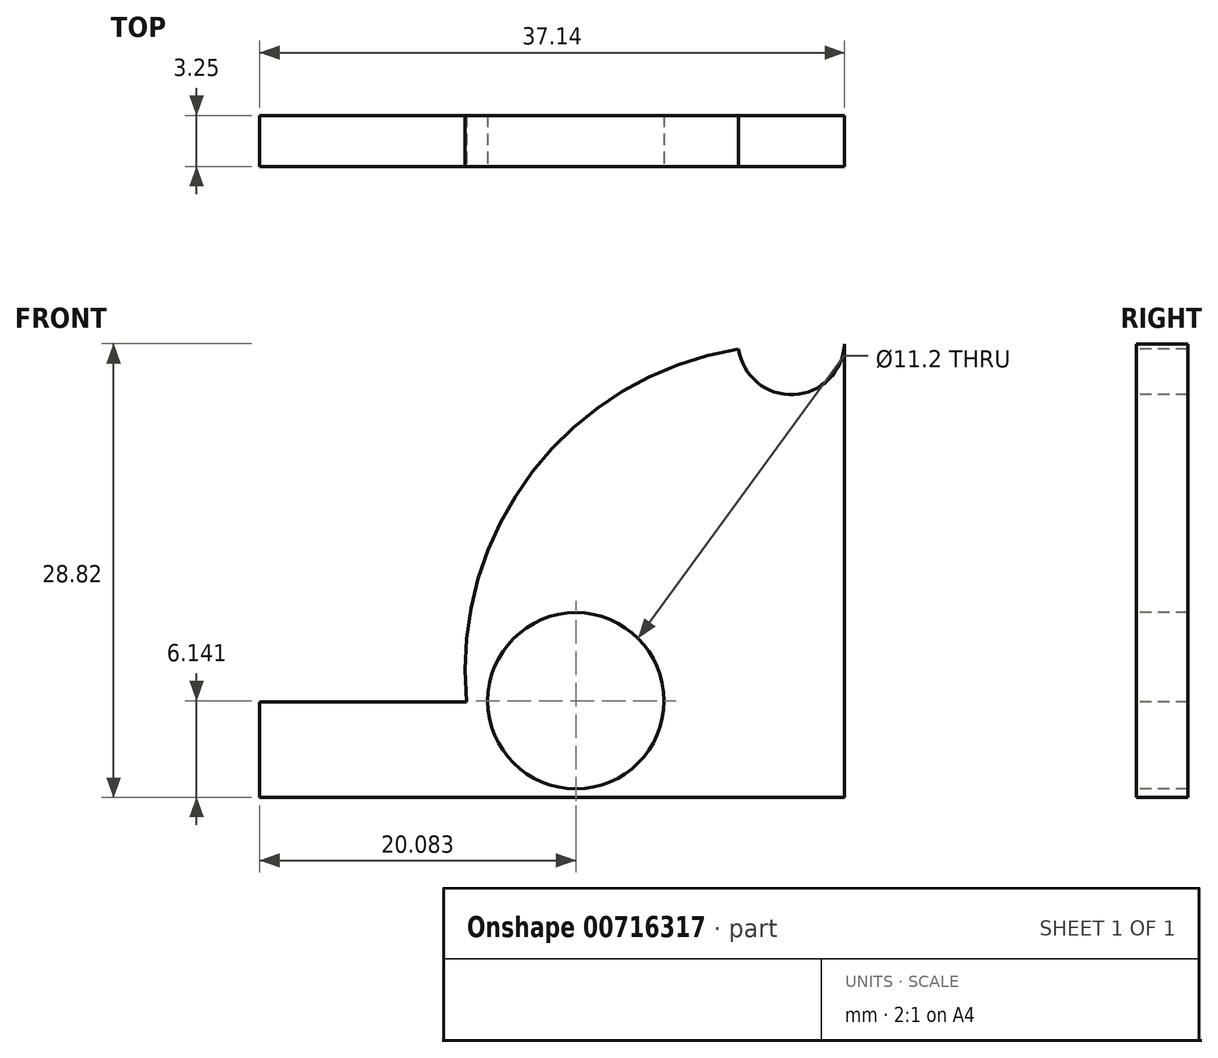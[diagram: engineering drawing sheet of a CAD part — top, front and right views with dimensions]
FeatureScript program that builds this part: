
annotation { "Feature Type Name" : "Feature", "Feature Type Description" : "" }
export const myFeature = defineFeature(function(context is Context, id is Id, definition is map)
    precondition{}
    {
        {
            var Q0;
            Q0=qCreatedBy(makeId("Front.planeOp"),FACE);
            var sketch = newSketch(context, id + "F0", { "sketchPlane" : qUnion([Q0])});
            skLineSegment(sketch, "E0", {"start": v(-17.05, -6.06) * mm, "end": v(20.1, -6.06) * mm});
            skLineSegment(sketch, "E1", {"start": v(20.1, -6.06) * mm, "end": v(20.1, 22.76) * mm});
            skLineSegment(sketch, "E2", {"start": v(-17.05, -6.06) * mm, "end": v(-17.05, 0) * mm});
            skLineSegment(sketch, "E3", {"start": v(-17.05, 0) * mm, "end": v(-3.92, 0) * mm});
            skArc(sketch, "E4", {"start": v(13.37, 22.44) * mm, "mid": v(0.29, 14.64) * mm, "end": v(-3.92, 0) * mm});
            skCircle(sketch, "E5", {"center": v(16.72, 22.9) * mm, "radius": 3.38 * mm});
            skPoint(sketch, "E5.third.point", {"position": v(16.9, 26.28) * mm});
            skFitSpline(sketch, "E6", {"points": [v(12.39, 22.25) * mm, v(14.8, 18.64) * mm, v(18.5, 18.19) * mm, v(20.1, 16.75) * mm], "startDerivative": vector(4.83, -12.05) * mm, "endDerivative": vector(4.66, -6.77) * mm});
            skLineSegment(sketch, "E7.bottom", {"start": v(-17.05, -0.6) * mm, "end": v(-16.21, -0.6) * mm});
            skLineSegment(sketch, "E7.top", {"start": v(-17.05, -5.27) * mm, "end": v(-16.21, -5.27) * mm});
            skLineSegment(sketch, "E7.left", {"start": v(-17.05, -0.6) * mm, "end": v(-17.05, -5.27) * mm});
            skLineSegment(sketch, "E7.right", {"start": v(-16.21, -0.6) * mm, "end": v(-16.21, -5.27) * mm});
            skCircle(sketch, "E8", {"center": v(3.03, 0.08) * mm, "radius": 5.6 * mm});
            skPoint(sketch, "E8.first.point", {"position": v(-2.56, 0) * mm});
            skPoint(sketch, "E8.second.point", {"position": v(8.63, 0) * mm});
            skPoint(sketch, "E8.third.point", {"position": v(5.15, 5.26) * mm});
            skCircle(sketch, "E9", {"center": v(3.03, 0.07) * mm, "radius": 4.71 * mm});
            skSolve(sketch);
        }
        {
            var Q0;
            Q0=makeQuery(id+"F0.imprint","IMPRINT",FACE,{"disambiguationData":[TD([[makeQuery(id+"F0.imprint","IMPRINT",EDGE,{"derivedFrom":sQuery(id+"F0.wireOp",EDGE,"E7.bottom")}),-1.0]])]});
            var Q1;
            {var subQ4=sQuery(id+"F0.wireOp",EDGE,"E0");Q1=makeQuery(id+"F0.imprint","IMPRINT",FACE,{"disambiguationData":[TD([[makeQuery(id+"F0.imprint","IMPRINT",EDGE,{"derivedFrom":subQ4}),1.0]])]});}
            var Q2;
            {var subQ3=sQuery(id+"F0.wireOp",EDGE,"E6");Q2=makeQuery(id+"F0.imprint","IMPRINT",FACE,{"disambiguationData":[TD([[makeQuery(id+"F0.imprint","IMPRINT",EDGE,{"derivedFrom":subQ3}),1.0]])]});}
            extrude(context, id + "F1", {"entities" : qUnion([Q0, Q1, Q2]), "oppositeDirection" : true, "depth" : 3.25 * mm, "offsetDistance" : 25.4 * mm});
        }
    });
